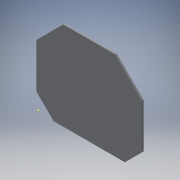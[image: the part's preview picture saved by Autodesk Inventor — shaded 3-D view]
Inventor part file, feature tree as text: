
AUTODESK INVENTOR PART (.ipt)
format: ipt  version: 2016 (Build 200138000, 138)  size: 102,912 bytes
history: native  units: in
note: dims shown in document units (in); Inventor stores cm internally (conversion verified against a paired STEP export)
features: chamfer x4, sketch x2, extrude x1, direct_edit x1, move_body x1
ambient origin geometry x8: Origin, YZ Plane, XZ Plane, XY Plane, X Axis, Y Axis, Z Axis, Center Point
bodies: Solid1 (feature_tree)
feature tree (9):
  extrude  "Extrusion1"  Depth=6.957in
  chamfer  "Chamfer1"  Distance=0.15in
  chamfer  "Chamfer2"  Distance=1.5in Angle=45.0deg
  chamfer  "Chamfer3"  Distance=1.5in Angle=45.0deg
  chamfer  "Chamfer4"  Distance=1.5in Angle=45.0deg
  direct_edit  "Direct Edit1"
  sketch  "Sketch2"  dims[d13=1.5in d14=0.125in d15=45.0deg d16=0.0in d17=0.0in d18=0.87in]
  sketch  "Sketch1"  dims[d0=9.308in d1=6.957in d2=0.15in d3=0.0in d4=1.5in d5=0.125in d6=45.0deg d7=1.5in d8=0.125in d9=45.0deg d10=1.5in d11=0.125in d12=45.0deg]
  move_body  "Move1"
